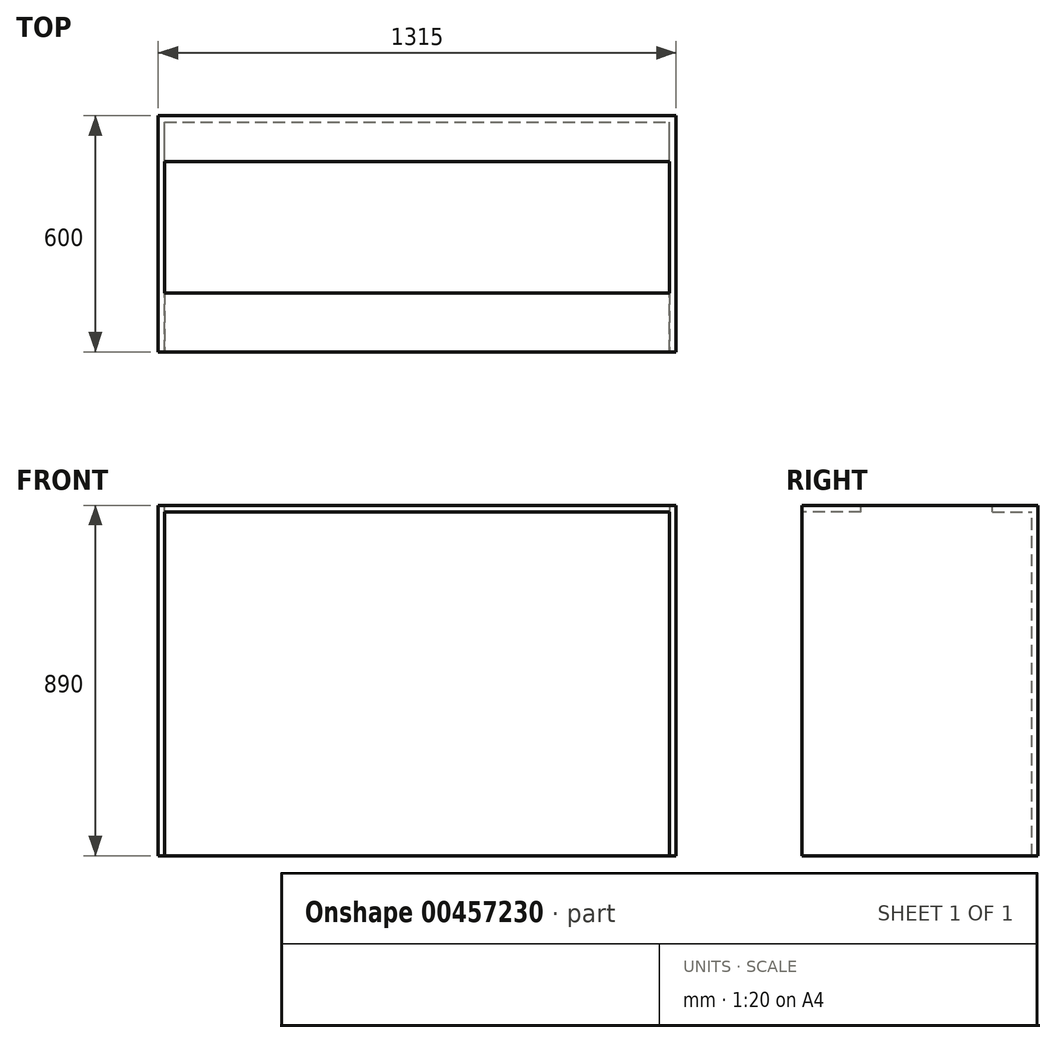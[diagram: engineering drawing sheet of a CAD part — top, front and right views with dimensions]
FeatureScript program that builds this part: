
annotation { "Feature Type Name" : "Feature", "Feature Type Description" : "" }
export const myFeature = defineFeature(function(context is Context, id is Id, definition is map)
    precondition{}
    {
        {
            var Q0;
            Q0=qCreatedBy(makeId("Front.planeOp"),FACE);
            var sketch = newSketch(context, id + "F0", { "sketchPlane" : qUnion([Q0])});
            skLineSegment(sketch, "E0.bottom", {"start": v(0, 0) * mm, "end": v(-1315, 0) * mm});
            skLineSegment(sketch, "E0.top", {"start": v(0, 890) * mm, "end": v(-1315, 890) * mm});
            skLineSegment(sketch, "E0.left", {"start": v(0, 0) * mm, "end": v(0, 890) * mm});
            skLineSegment(sketch, "E0.right", {"start": v(-1315, 0) * mm, "end": v(-1315, 890) * mm});
            skLineSegment(sketch, "E1", {"start": v(-1299, 0) * mm, "end": v(-1299, 874) * mm});
            skLineSegment(sketch, "E2", {"start": v(-1299, 874) * mm, "end": v(-16, 874) * mm});
            skLineSegment(sketch, "E3", {"start": v(-16, 874) * mm, "end": v(-16, 0) * mm});
            skLineSegment(sketch, "E4", {"start": v(-1299, 874) * mm, "end": v(-1299, 890) * mm});
            skLineSegment(sketch, "E5", {"start": v(-16, 874) * mm, "end": v(-16, 890) * mm});
            skSolve(sketch);
        }
        {
            var Q0;
            {var subQ0=sQuery(id+"F0.wireOp",EDGE,"E1");Q0=makeQuery(id+"F0.imprint","IMPRINT",FACE,{"disambiguationData":[TD([[makeQuery(id+"F0.imprint","IMPRINT",EDGE,{"derivedFrom":subQ0}),-1.0]])]});}
            var Q1;
            Q1=makeQuery(id+"F0.imprint","IMPRINT",FACE,{"disambiguationData":[TD([[makeQuery(id+"F0.imprint","IMPRINT",EDGE,{"derivedFrom":sQuery(id+"F0.wireOp",EDGE,"E0.top")}),1.0]])]});
            var Q2;
            {var subQ0=sQuery(id+"F0.wireOp",EDGE,"E0.left");Q2=makeQuery(id+"F0.imprint","IMPRINT",FACE,{"disambiguationData":[TD([[makeQuery(id+"F0.imprint","IMPRINT",EDGE,{"derivedFrom":subQ0}),1.0]])]});}
            var Q3;
            {var subQ1=sQuery(id+"F0.wireOp",EDGE,"E0.right");Q3=makeQuery(id+"F0.imprint","IMPRINT",FACE,{"disambiguationData":[TD([[makeQuery(id+"F0.imprint","IMPRINT",EDGE,{"derivedFrom":subQ1}),-1.0]])]});}
            extrude(context, id + "F1", {"entities" : qUnion([Q0, Q1, Q2, Q3]), "oppositeDirection" : true, "depth" : 16 * mm});
        }
        {
            var Q0;
            {var subQ1=sQuery(id+"F0.wireOp",EDGE,"E0.right");Q0=makeQuery(id+"F0.imprint","IMPRINT",FACE,{"disambiguationData":[TD([[makeQuery(id+"F0.imprint","IMPRINT",EDGE,{"derivedFrom":subQ1}),-1.0]])]});}
            var Q1;
            {var subQ0=sQuery(id+"F0.wireOp",EDGE,"E0.left");Q1=makeQuery(id+"F0.imprint","IMPRINT",FACE,{"disambiguationData":[TD([[makeQuery(id+"F0.imprint","IMPRINT",EDGE,{"derivedFrom":subQ0}),1.0]])]});}
            extrude(context, id + "F2", {"entities" : qUnion([Q0, Q1]), "operationType" : NewBodyOperationType.ADD, "depth" : 584 * mm});
        }
        {
            var Q0;
            Q0=makeQuery(id+"F0.imprint","IMPRINT",FACE,{"disambiguationData":[TD([[makeQuery(id+"F0.imprint","IMPRINT",EDGE,{"derivedFrom":sQuery(id+"F0.wireOp",EDGE,"E2")}),1.0]])]});
            extrude(context, id + "F3", {"entities" : qUnion([Q0]), "operationType" : NewBodyOperationType.ADD, "depth" : 100 * mm});
        }
        {
            var Q0;
            Q0=makeQuery(id+"F2.opExtrude","CAP_FACE",FACE,{"disambiguationData":[OSD([sQuery(id+"F0.wireOp",EDGE,"E0.bottom"),sQuery(id+"F0.wireOp",EDGE,"E0.top"),sQuery(id+"F0.wireOp",EDGE,"E0.right"),sQuery(id+"F0.wireOp",EDGE,"E1"),sQuery(id+"F0.wireOp",EDGE,"E4")])],"isStart":false});
            var sketch = newSketch(context, id + "F4", { "sketchPlane" : qUnion([Q0])});
            skPoint(sketch, "E6.0", {"position": v(-1299, 890) * mm});
            skLineSegment(sketch, "E7.bottom", {"start": v(-1299, 890) * mm, "end": v(-16, 890) * mm});
            skLineSegment(sketch, "E7.top", {"start": v(-1299, 874) * mm, "end": v(-16, 874) * mm});
            skLineSegment(sketch, "E7.left", {"start": v(-1299, 890) * mm, "end": v(-1299, 874) * mm});
            skLineSegment(sketch, "E7.right", {"start": v(-16, 890) * mm, "end": v(-16, 874) * mm});
            skPoint(sketch, "E8.0", {"position": v(-16, 890) * mm});
            skSolve(sketch);
        }
        {
            var Q0;
            Q0=makeQuery(id+"F4.imprint","IMPRINT",FACE,{"disambiguationData":[TD([[makeQuery(id+"F4.imprint","IMPRINT",EDGE,{"derivedFrom":sQuery(id+"F4.wireOp",EDGE,"E7.bottom")}),-1.0]])]});
            extrude(context, id + "F5", {"entities" : qUnion([Q0]), "operationType" : NewBodyOperationType.ADD, "oppositeDirection" : true, "depth" : 150 * mm});
        }
    });
